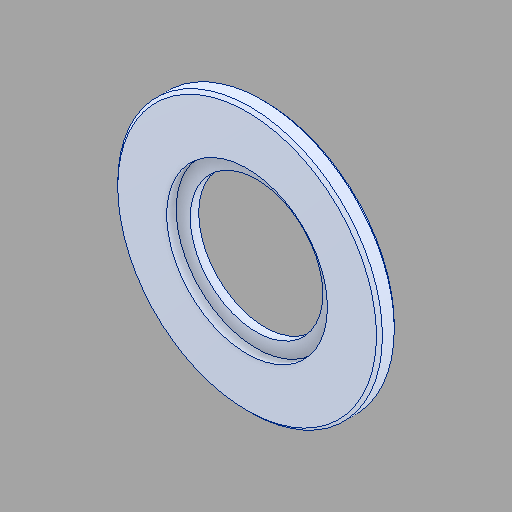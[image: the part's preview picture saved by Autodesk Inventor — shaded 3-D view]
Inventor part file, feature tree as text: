
AUTODESK INVENTOR PART (.ipt)
format: ipt  version: 2024.2 (Build 282272000, 272)  size: 112,640 bytes
history: native  units: in
note: dims shown in document units (in); Inventor stores cm internally (conversion verified against a paired STEP export)
features: chamfer x1
ambient origin geometry x8: Origin, YZ Plane, XZ Plane, XY Plane, X Axis, Y Axis, Z Axis, Center Point
bodies: Solid1 (feature_tree)
feature tree (1):
  chamfer  "Chamfer1"  [1 undecoded]
note: 1 required parameter value undecoded (feature->parameter linkage not recoverable at this tier; creation-order binding heuristic only, values carry confidence <= 0.55)
